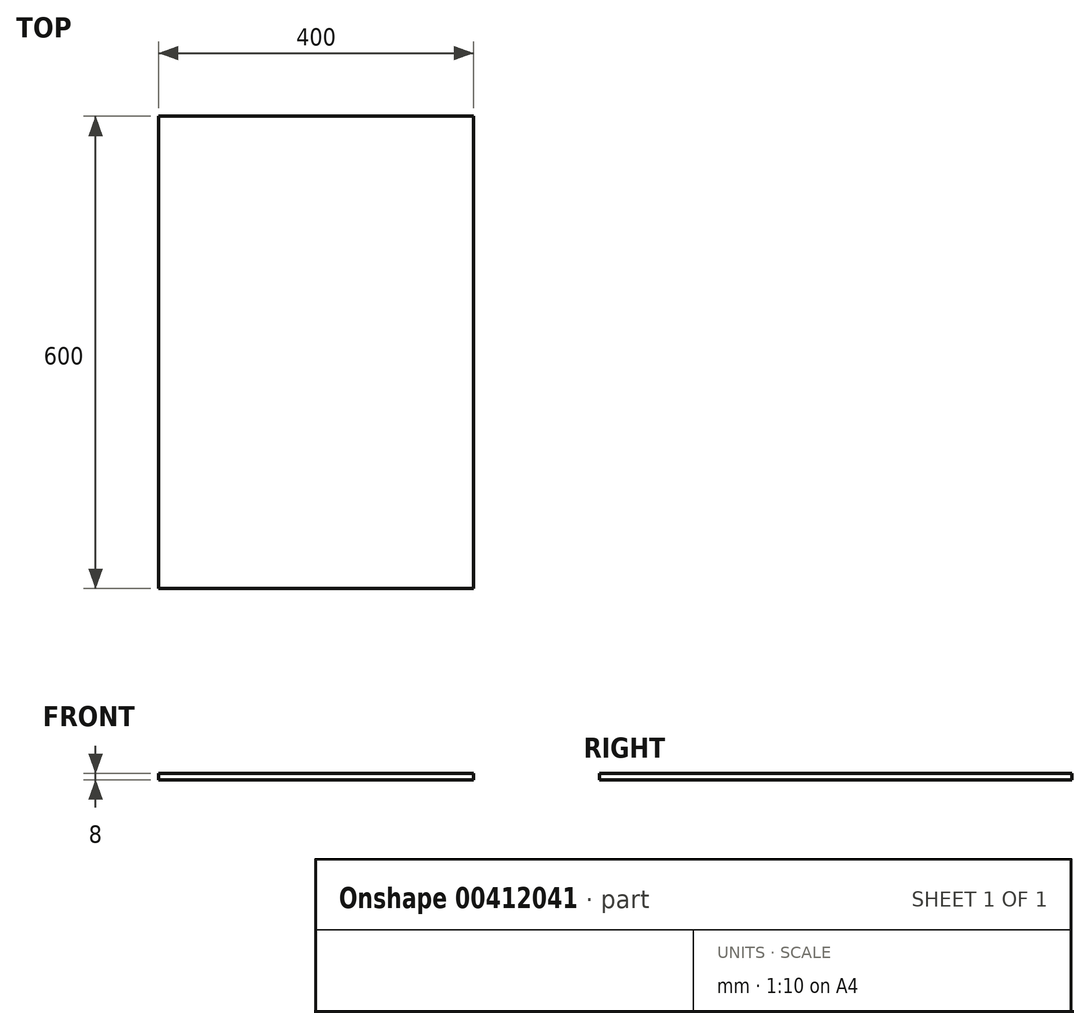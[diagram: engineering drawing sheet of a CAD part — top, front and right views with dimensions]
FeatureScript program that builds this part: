
annotation { "Feature Type Name" : "Feature", "Feature Type Description" : "" }
export const myFeature = defineFeature(function(context is Context, id is Id, definition is map)
    precondition{}
    {
        {
            var Q0;
            Q0=qCreatedBy(makeId("Top.planeOp"),FACE);
            var sketch = newSketch(context, id + "F0", { "sketchPlane" : qUnion([Q0])});
            skLineSegment(sketch, "E0.bottom", {"start": v(200, 300) * mm, "end": v(-200, 300) * mm});
            skLineSegment(sketch, "E0.top", {"start": v(200, -300) * mm, "end": v(-200, -300) * mm});
            skLineSegment(sketch, "E0.left", {"start": v(200, 300) * mm, "end": v(200, -300) * mm});
            skLineSegment(sketch, "E0.right", {"start": v(-200, 300) * mm, "end": v(-200, -300) * mm});
            skPoint(sketch, "E0.middle", {"position": v(0, 0) * mm});
            skSolve(sketch);
        }
        {
            var Q0;
            Q0 = qSketchRegion(id + "F0", true);
            extrude(context, id + "F1", {"entities" : qUnion([Q0]), "depth" : 8 * mm});
        }
    });
